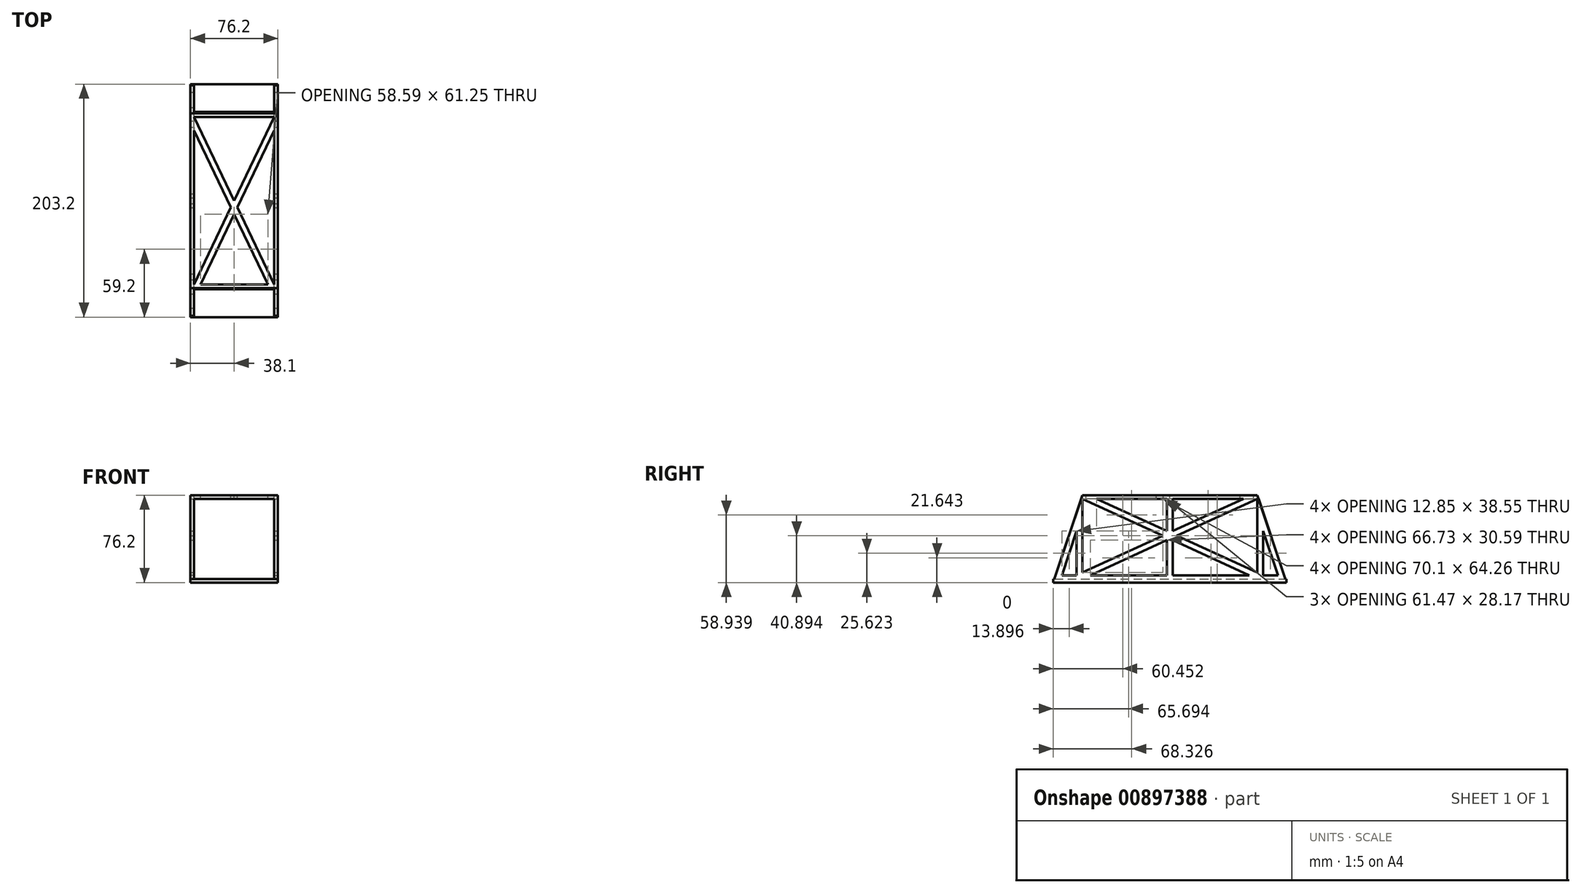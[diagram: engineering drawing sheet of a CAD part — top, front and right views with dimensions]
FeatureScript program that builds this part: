
annotation { "Feature Type Name" : "Feature", "Feature Type Description" : "" }
export const myFeature = defineFeature(function(context is Context, id is Id, definition is map)
    precondition{}
    {
        {
            var Q0;
            Q0=qCreatedBy(makeId("Right.planeOp"),FACE);
            var sketch = newSketch(context, id + "F0", { "sketchPlane" : qUnion([Q0])});
            skLineSegment(sketch, "E0", {"start": v(-101.6, -38.1) * mm, "end": v(101.6, -38.1) * mm});
            skLineSegment(sketch, "E1", {"start": v(-76.2, 38.1) * mm, "end": v(76.2, 38.1) * mm});
            skLineSegment(sketch, "E2", {"start": v(76.2, 38.1) * mm, "end": v(101.6, -38.1) * mm});
            skLineSegment(sketch, "E3", {"start": v(-76.2, 38.1) * mm, "end": v(-101.6, -38.1) * mm});
            skSolve(sketch);
        }
        {
            var Q0;
            Q0 = qSketchRegion(id + "F0", true);
            extrude(context, id + "F1", {"entities" : qUnion([Q0]), "endBound" : BoundingType.SYMMETRIC, "depth" : 76.2 * mm, "offsetDistance" : 25.4 * mm});
        }
        {
            var Q0;
            Q0=qCreatedBy(makeId("Front.planeOp"),FACE);
            var sketch = newSketch(context, id + "F2", { "sketchPlane" : qUnion([Q0])});
            skLineSegment(sketch, "E4.bottom", {"start": v(34.93, -34.92) * mm, "end": v(-34.93, -34.92) * mm});
            skLineSegment(sketch, "E4.top", {"start": v(34.93, 34.93) * mm, "end": v(-34.93, 34.92) * mm});
            skLineSegment(sketch, "E4.left", {"start": v(34.93, -34.92) * mm, "end": v(34.93, 34.92) * mm});
            skLineSegment(sketch, "E4.right", {"start": v(-34.93, -34.92) * mm, "end": v(-34.93, 34.92) * mm});
            skPoint(sketch, "E4.middle", {"position": v(0, 0) * mm});
            skSolve(sketch);
        }
        {
            var Q0;
            Q0 = qSketchRegion(id + "F2", true);
            extrude(context, id + "F3", {"entities" : qUnion([Q0]), "operationType" : NewBodyOperationType.REMOVE, "endBound" : BoundingType.SYMMETRIC, "depth" : 254 * mm, "offsetDistance" : 25.4 * mm});
        }
        {
            var Q0;
            Q0=makeQuery(id+"F1.opExtrude","CAP_FACE",FACE,{"disambiguationData":[OSD([sQuery(id+"F0.wireOp",EDGE,"E0"),sQuery(id+"F0.wireOp",EDGE,"E1"),sQuery(id+"F0.wireOp",EDGE,"E2"),sQuery(id+"F0.wireOp",EDGE,"E3")])],"isStart":false});
            var sketch = newSketch(context, id + "F4", { "sketchPlane" : qUnion([Q0])});
            skLineSegment(sketch, "E5.bottom", {"start": v(76.2, -34.92) * mm, "end": v(-76.2, -34.92) * mm});
            skLineSegment(sketch, "E5.top", {"start": v(76.2, 34.92) * mm, "end": v(-76.2, 34.92) * mm});
            skLineSegment(sketch, "E5.left", {"start": v(76.2, -34.92) * mm, "end": v(76.2, 34.92) * mm});
            skLineSegment(sketch, "E5.right", {"start": v(-76.2, -34.92) * mm, "end": v(-76.2, 34.92) * mm});
            skPoint(sketch, "E5.middle", {"position": v(0, 0) * mm});
            skLineSegment(sketch, "E6", {"start": v(-81.28, -34.92) * mm, "end": v(-81.28, 6.8) * mm});
            skLineSegment(sketch, "E7", {"start": v(-81.28, 6.8) * mm, "end": v(-95.19, -34.93) * mm});
            skLineSegment(sketch, "E8", {"start": v(-95.19, -34.92) * mm, "end": v(-81.28, -34.92) * mm});
            skLineSegment(sketch, "E9.MirrorCS", {"start": v(81.28, -34.92) * mm, "end": v(81.28, 6.8) * mm});
            skLineSegment(sketch, "E10.MirrorCS", {"start": v(81.28, 6.8) * mm, "end": v(95.19, -34.93) * mm});
            skLineSegment(sketch, "E11.MirrorCS", {"start": v(95.19, -34.92) * mm, "end": v(81.28, -34.92) * mm});
            skLineSegment(sketch, "E12", {"start": v(-76.2, 34.92) * mm, "end": v(76.2, -34.92) * mm});
            skLineSegment(sketch, "E13", {"start": v(76.2, 34.92) * mm, "end": v(-76.2, -34.92) * mm});
            skLineSegment(sketch, "E14", {"start": v(-76.2, -29.34) * mm, "end": v(64, 34.93) * mm});
            skLineSegment(sketch, "E15", {"start": v(76.2, -29.34) * mm, "end": v(-64, 34.92) * mm});
            skLineSegment(sketch, "E16.bottom", {"start": v(2.54, -34.92) * mm, "end": v(-2.54, -34.92) * mm});
            skLineSegment(sketch, "E16.top", {"start": v(2.54, 34.92) * mm, "end": v(-2.54, 34.92) * mm});
            skLineSegment(sketch, "E16.left", {"start": v(2.54, -34.93) * mm, "end": v(2.54, 34.93) * mm});
            skLineSegment(sketch, "E16.right", {"start": v(-2.54, -34.93) * mm, "end": v(-2.54, 34.93) * mm});
            skSolve(sketch);
        }
        {
            var Q0;
            Q0=makeQuery(id+"F4.imprint","IMPRINT",FACE,{"disambiguationData":[TD([[makeQuery(id+"F4.imprint","IMPRINT",EDGE,{"derivedFrom":sQuery(id+"F4.wireOp",EDGE,"E6")}),1.0]])]});
            var Q1;
            {var subQ1=sQuery(id+"F4.wireOp",EDGE,"E5.right");var subQ3=sQuery(id+"F4.wireOp",EDGE,"E14");var subQ4=makeQuery(id+"F4.imprint","INTERSECT",VERTEX,{"derivedFrom":[subQ1,subQ3]});Q1=makeQuery(id+"F4.imprint","IMPRINT",FACE,{"disambiguationData":[TD([[makeQuery(id+"F4.imprint","IMPRINT",EDGE,{"disambiguationData":[TD([[subQ4,-1.0]])],"derivedFrom":subQ3}),1.0]])]});}
            var Q2;
            {var subQ0=sQuery(id+"F4.wireOp",EDGE,"E15");var subQ1=sQuery(id+"F4.wireOp",EDGE,"E5.top");var subQ2=makeQuery(id+"F4.imprint","INTERSECT",VERTEX,{"derivedFrom":[subQ1,subQ0]});Q2=makeQuery(id+"F4.imprint","IMPRINT",FACE,{"disambiguationData":[TD([[makeQuery(id+"F4.imprint","IMPRINT",EDGE,{"disambiguationData":[TD([[subQ2,1.0]])],"derivedFrom":subQ0}),-1.0]])]});}
            var Q3;
            {var subQ0=sQuery(id+"F4.wireOp",EDGE,"E14");var subQ1=sQuery(id+"F4.wireOp",EDGE,"E5.top");var subQ2=makeQuery(id+"F4.imprint","INTERSECT",VERTEX,{"derivedFrom":[subQ1,subQ0]});Q3=makeQuery(id+"F4.imprint","IMPRINT",FACE,{"disambiguationData":[TD([[makeQuery(id+"F4.imprint","IMPRINT",EDGE,{"disambiguationData":[TD([[subQ2,1.0]])],"derivedFrom":subQ0}),1.0]])]});}
            var Q4;
            {var subQ1=sQuery(id+"F4.wireOp",EDGE,"E5.left");var subQ3=sQuery(id+"F4.wireOp",EDGE,"E15");var subQ4=makeQuery(id+"F4.imprint","INTERSECT",VERTEX,{"derivedFrom":[subQ1,subQ3]});Q4=makeQuery(id+"F4.imprint","IMPRINT",FACE,{"disambiguationData":[TD([[makeQuery(id+"F4.imprint","IMPRINT",EDGE,{"disambiguationData":[TD([[subQ4,-1.0]])],"derivedFrom":subQ3}),-1.0]])]});}
            var Q5;
            Q5=makeQuery(id+"F4.imprint","IMPRINT",FACE,{"disambiguationData":[TD([[makeQuery(id+"F4.imprint","IMPRINT",EDGE,{"derivedFrom":sQuery(id+"F4.wireOp",EDGE,"E9.MirrorCS")}),-1.0]])]});
            var Q6;
            {var subQ0=sQuery(id+"F4.wireOp",EDGE,"E12");var subQ3=sQuery(id+"F4.wireOp",EDGE,"E16.left");var subQ5=makeQuery(id+"F4.imprint","INTERSECT",VERTEX,{"derivedFrom":[subQ0,subQ3]});Q6=makeQuery(id+"F4.imprint","IMPRINT",FACE,{"disambiguationData":[TD([[makeQuery(id+"F4.imprint","IMPRINT",EDGE,{"disambiguationData":[TD([[subQ5,-1.0]])],"derivedFrom":subQ0}),-1.0]])]});}
            var Q7;
            {var subQ0=sQuery(id+"F4.wireOp",EDGE,"E13");var subQ3=sQuery(id+"F4.wireOp",EDGE,"E16.right");var subQ5=makeQuery(id+"F4.imprint","INTERSECT",VERTEX,{"derivedFrom":[subQ0,subQ3]});Q7=makeQuery(id+"F4.imprint","IMPRINT",FACE,{"disambiguationData":[TD([[makeQuery(id+"F4.imprint","IMPRINT",EDGE,{"disambiguationData":[TD([[subQ5,-1.0]])],"derivedFrom":subQ0}),1.0]])]});}
            extrude(context, id + "F5", {"entities" : qUnion([Q0, Q1, Q2, Q3, Q4, Q5, Q6, Q7]), "operationType" : NewBodyOperationType.REMOVE, "oppositeDirection" : true, "depth" : 76.2 * mm, "offsetDistance" : 25.4 * mm});
        }
        {
            var Q0;
            Q0=makeQuery(id+"F1.opExtrude","SWEPT_FACE",FACE,{"disambiguationData":[OSD([sQuery(id+"F0.wireOp",EDGE,"E1")])]});
            var sketch = newSketch(context, id + "F6", { "sketchPlane" : qUnion([Q0])});
            skLineSegment(sketch, "E17.bottom", {"start": v(34.93, 73.03) * mm, "end": v(-34.93, 73.03) * mm});
            skLineSegment(sketch, "E17.top", {"start": v(34.93, -73.03) * mm, "end": v(-34.93, -73.03) * mm});
            skLineSegment(sketch, "E17.left", {"start": v(34.93, -73.03) * mm, "end": v(34.93, 73.03) * mm});
            skLineSegment(sketch, "E17.right", {"start": v(-34.93, -73.03) * mm, "end": v(-34.93, 73.03) * mm});
            skPoint(sketch, "E17.middle", {"position": v(0, 0) * mm});
            skLineSegment(sketch, "E18", {"start": v(-34.92, 73.02) * mm, "end": v(34.92, -73.02) * mm});
            skLineSegment(sketch, "E19", {"start": v(34.92, 73.02) * mm, "end": v(-34.92, -73.02) * mm});
            skLineSegment(sketch, "E20", {"start": v(-34.93, 61.25) * mm, "end": v(29.3, -73.03) * mm});
            skLineSegment(sketch, "E21", {"start": v(34.93, 61.25) * mm, "end": v(-29.3, -73.03) * mm});
            skSolve(sketch);
        }
        {
            var Q0;
            {var subQ1=sQuery(id+"F6.wireOp",EDGE,"E17.right");var subQ3=sQuery(id+"F6.wireOp",EDGE,"E20");var subQ4=makeQuery(id+"F6.imprint","INTERSECT",VERTEX,{"derivedFrom":[subQ1,subQ3]});Q0=makeQuery(id+"F6.imprint","IMPRINT",FACE,{"disambiguationData":[TD([[makeQuery(id+"F6.imprint","IMPRINT",EDGE,{"disambiguationData":[TD([[subQ4,-1.0]])],"derivedFrom":subQ3}),-1.0]])]});}
            var Q1;
            {var subQ0=sQuery(id+"F6.wireOp",EDGE,"E17.bottom");Q1=makeQuery(id+"F6.imprint","IMPRINT",FACE,{"disambiguationData":[TD([[makeQuery(id+"F6.imprint","IMPRINT",EDGE,{"derivedFrom":subQ0}),1.0]])]});}
            var Q2;
            {var subQ1=sQuery(id+"F6.wireOp",EDGE,"E17.left");var subQ3=sQuery(id+"F6.wireOp",EDGE,"E21");var subQ4=makeQuery(id+"F6.imprint","INTERSECT",VERTEX,{"derivedFrom":[subQ1,subQ3]});Q2=makeQuery(id+"F6.imprint","IMPRINT",FACE,{"disambiguationData":[TD([[makeQuery(id+"F6.imprint","IMPRINT",EDGE,{"disambiguationData":[TD([[subQ4,-1.0]])],"derivedFrom":subQ3}),1.0]])]});}
            var Q3;
            {var subQ0=sQuery(id+"F6.wireOp",EDGE,"E20");var subQ1=sQuery(id+"F6.wireOp",EDGE,"E17.top");var subQ2=makeQuery(id+"F6.imprint","INTERSECT",VERTEX,{"derivedFrom":[subQ1,subQ0]});Q3=makeQuery(id+"F6.imprint","IMPRINT",FACE,{"disambiguationData":[TD([[makeQuery(id+"F6.imprint","IMPRINT",EDGE,{"disambiguationData":[TD([[subQ2,-1.0]])],"derivedFrom":subQ1}),-1.0]])]});}
            extrude(context, id + "F7", {"entities" : qUnion([Q0, Q1, Q2, Q3]), "operationType" : NewBodyOperationType.REMOVE, "oppositeDirection" : true, "depth" : 3.17 * mm, "offsetDistance" : 25.4 * mm});
        }
        {
            var Q0;
            Q0=makeQuery(id+"F1.opExtrude","CAP_FACE",FACE,{"disambiguationData":[OSD([sQuery(id+"F0.wireOp",EDGE,"E0"),sQuery(id+"F0.wireOp",EDGE,"E1"),sQuery(id+"F0.wireOp",EDGE,"E2"),sQuery(id+"F0.wireOp",EDGE,"E3")])],"isStart":false});
            var sketch = newSketch(context, id + "F8", { "sketchPlane" : qUnion([Q0])});
            skLineSegment(sketch, "E22.bottom", {"start": v(-101.6, -38.1) * mm, "end": v(-95.19, -38.1) * mm});
            skLineSegment(sketch, "E22.top", {"start": v(-101.6, -34.93) * mm, "end": v(-95.19, -34.93) * mm});
            skLineSegment(sketch, "E22.left", {"start": v(-101.6, -38.1) * mm, "end": v(-101.6, -34.93) * mm});
            skLineSegment(sketch, "E22.right", {"start": v(-95.19, -38.1) * mm, "end": v(-95.19, -34.93) * mm});
            skLineSegment(sketch, "E23.MirrorCS", {"start": v(101.6, -38.1) * mm, "end": v(101.6, -34.93) * mm});
            skLineSegment(sketch, "E24.MirrorCS", {"start": v(95.19, -38.1) * mm, "end": v(95.19, -34.93) * mm});
            skLineSegment(sketch, "E25.MirrorCS", {"start": v(101.6, -34.93) * mm, "end": v(95.19, -34.93) * mm});
            skLineSegment(sketch, "E26.MirrorCS", {"start": v(101.6, -38.1) * mm, "end": v(95.19, -38.1) * mm});
            skSolve(sketch);
        }
        {
            var Q0;
            Q0 = qSketchRegion(id + "F8", true);
            extrude(context, id + "F9", {"entities" : qUnion([Q0]), "operationType" : NewBodyOperationType.ADD, "oppositeDirection" : true, "depth" : 76.2 * mm, "offsetDistance" : 25.4 * mm});
        }
        {
            var Q0;
            {var subQ0=sQuery(id+"F4.wireOp",EDGE,"E5.bottom");Q0=makeQuery(id+"F9.boolean.opBoolean","MERGE",FACE,{"derivedFrom":[makeQuery(id+"F5.boolean.opBoolean","MERGE",FACE,{"derivedFrom":[makeQuery(id+"F3.boolean.opBoolean","COPY",FACE,{"derivedFrom":makeQuery(id+"F3.opExtrude","SWEPT_FACE",FACE,{"disambiguationData":[OSD([sQuery(id+"F2.wireOp",EDGE,"E4.bottom")])]})})],"fromTools":[makeQuery(id+"F5.opExtrude","SWEPT_FACE",FACE,{"disambiguationData":[OSD([subQ0]),TDD([makeQuery(id+"F4.imprint","IMPRINT",EDGE,{"disambiguationData":[TD([[makeQuery(id+"F4.imprint","INTERSECT",VERTEX,{"derivedFrom":[subQ0,sQuery(id+"F4.wireOp",EDGE,"E5.left"),sQuery(id+"F4.wireOp",EDGE,"E12")]}),-1.0]])],"derivedFrom":subQ0})])]}),makeQuery(id+"F5.opExtrude","SWEPT_FACE",FACE,{"disambiguationData":[OSD([subQ0]),TDD([makeQuery(id+"F4.imprint","IMPRINT",EDGE,{"disambiguationData":[TD([[makeQuery(id+"F4.imprint","INTERSECT",VERTEX,{"derivedFrom":[subQ0,sQuery(id+"F4.wireOp",EDGE,"E5.right"),sQuery(id+"F4.wireOp",EDGE,"E13")]}),1.0]])],"derivedFrom":subQ0})])]}),makeQuery(id+"F5.opExtrude","SWEPT_FACE",FACE,{"disambiguationData":[OSD([sQuery(id+"F4.wireOp",EDGE,"E8")])]}),makeQuery(id+"F5.opExtrude","SWEPT_FACE",FACE,{"disambiguationData":[OSD([sQuery(id+"F4.wireOp",EDGE,"E11.MirrorCS")])]})]}),makeQuery(id+"F9.opExtrude","SWEPT_FACE",FACE,{"disambiguationData":[OSD([sQuery(id+"F8.wireOp",EDGE,"E22.top")])]}),makeQuery(id+"F9.opExtrude","SWEPT_FACE",FACE,{"disambiguationData":[OSD([sQuery(id+"F8.wireOp",EDGE,"E25.MirrorCS")])]})]});}
            var sketch = newSketch(context, id + "F10", { "sketchPlane" : qUnion([Q0])});
            skLineSegment(sketch, "E27.bottom", {"start": v(38.1, -95.19) * mm, "end": v(34.92, -95.19) * mm});
            skLineSegment(sketch, "E27.top", {"start": v(38.1, 95.19) * mm, "end": v(34.92, 95.19) * mm});
            skLineSegment(sketch, "E27.left", {"start": v(38.1, -95.19) * mm, "end": v(38.1, 95.19) * mm});
            skLineSegment(sketch, "E27.right", {"start": v(34.92, -95.19) * mm, "end": v(34.92, 95.19) * mm});
            skLineSegment(sketch, "E28.MirrorCS", {"start": v(-34.92, -95.19) * mm, "end": v(-34.92, 95.19) * mm});
            skLineSegment(sketch, "E29.MirrorCS", {"start": v(-38.1, -95.19) * mm, "end": v(-38.1, 95.19) * mm});
            skLineSegment(sketch, "E30.MirrorCS", {"start": v(-38.1, -95.19) * mm, "end": v(-34.92, -95.19) * mm});
            skLineSegment(sketch, "E31.MirrorCS", {"start": v(-38.1, 95.19) * mm, "end": v(-34.92, 95.19) * mm});
            skSolve(sketch);
        }
        {
            var Q0;
            Q0 = qSketchRegion(id + "F10", true);
            extrude(context, id + "F11", {"entities" : qUnion([Q0]), "operationType" : NewBodyOperationType.ADD, "depth" : 3.17 * mm, "offsetDistance" : 25.4 * mm});
        }
    });
